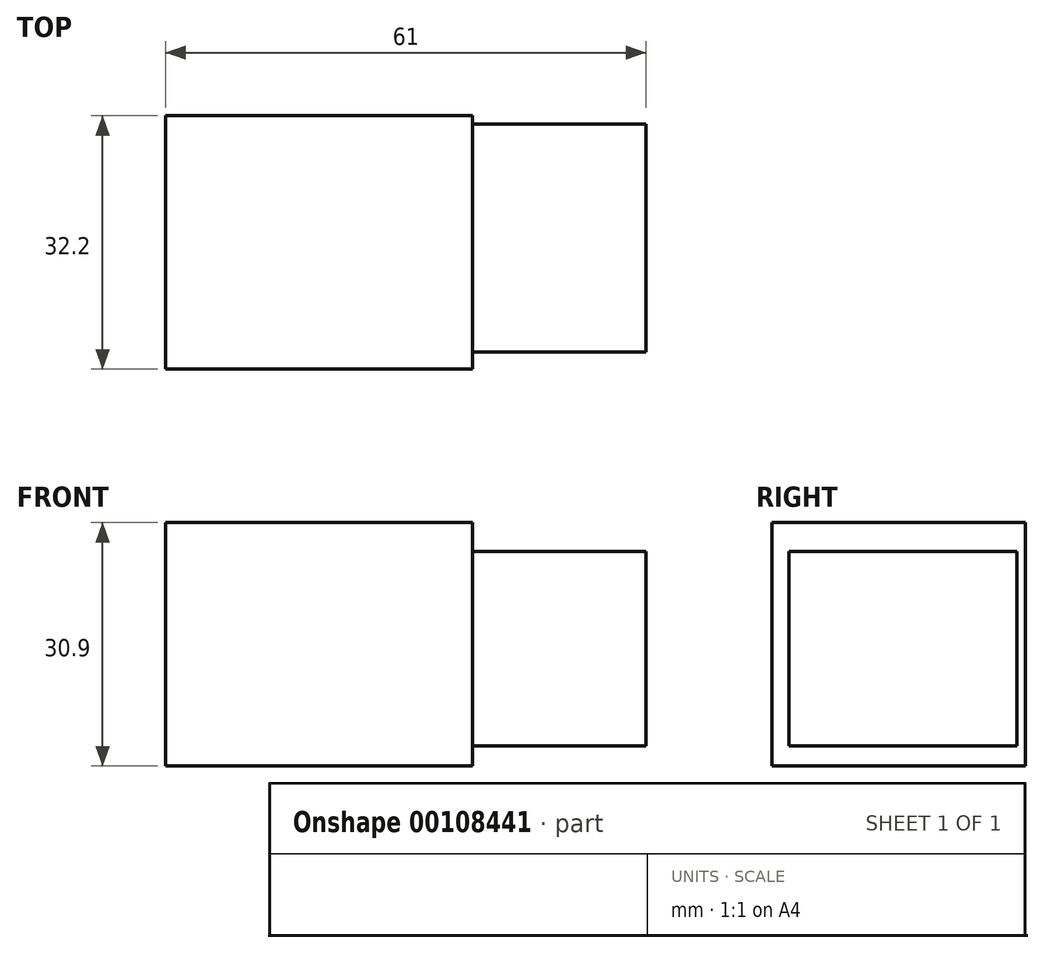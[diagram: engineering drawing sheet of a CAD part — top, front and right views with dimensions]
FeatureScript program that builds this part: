
annotation { "Feature Type Name" : "Feature", "Feature Type Description" : "" }
export const myFeature = defineFeature(function(context is Context, id is Id, definition is map)
    precondition{}
    {
        {
            var Q0;
            Q0=qCreatedBy(makeId("Top.planeOp"),FACE);
            var sketch = newSketch(context, id + "F0", { "sketchPlane" : qUnion([Q0])});
            skLineSegment(sketch, "E0.bottom", {"start": v(-19.98, 23.33) * mm, "end": v(19.02, 23.33) * mm});
            skLineSegment(sketch, "E0.top", {"start": v(-19.98, -8.87) * mm, "end": v(19.02, -8.87) * mm});
            skLineSegment(sketch, "E0.left", {"start": v(-19.98, 23.33) * mm, "end": v(-19.98, -8.87) * mm});
            skLineSegment(sketch, "E0.right", {"start": v(19.02, 23.33) * mm, "end": v(19.02, -8.87) * mm});
            skSolve(sketch);
        }
        {
            var Q0;
            Q0 = qSketchRegion(id + "F0", true);
            extrude(context, id + "F1", {"entities" : qUnion([Q0]), "depth" : 30.9 * mm});
        }
        {
            var Q0;
            Q0=makeQuery(id+"F1.opExtrude","SWEPT_FACE",FACE,{"disambiguationData":[OSD([sQuery(id+"F0.wireOp",EDGE,"E0.right")])]});
            var sketch = newSketch(context, id + "F2", { "sketchPlane" : qUnion([Q0])});
            skLineSegment(sketch, "E1.bottom", {"start": v(-6.72, 2.55) * mm, "end": v(22.28, 2.55) * mm});
            skLineSegment(sketch, "E1.top", {"start": v(-6.72, 27.25) * mm, "end": v(22.28, 27.25) * mm});
            skLineSegment(sketch, "E1.left", {"start": v(-6.72, 2.55) * mm, "end": v(-6.72, 27.25) * mm});
            skLineSegment(sketch, "E1.right", {"start": v(22.28, 2.55) * mm, "end": v(22.28, 27.25) * mm});
            skSolve(sketch);
        }
        {
            var Q0;
            Q0 = qSketchRegion(id + "F2", true);
            extrude(context, id + "F3", {"entities" : qUnion([Q0]), "operationType" : NewBodyOperationType.ADD, "depth" : 22 * mm});
        }
    });
